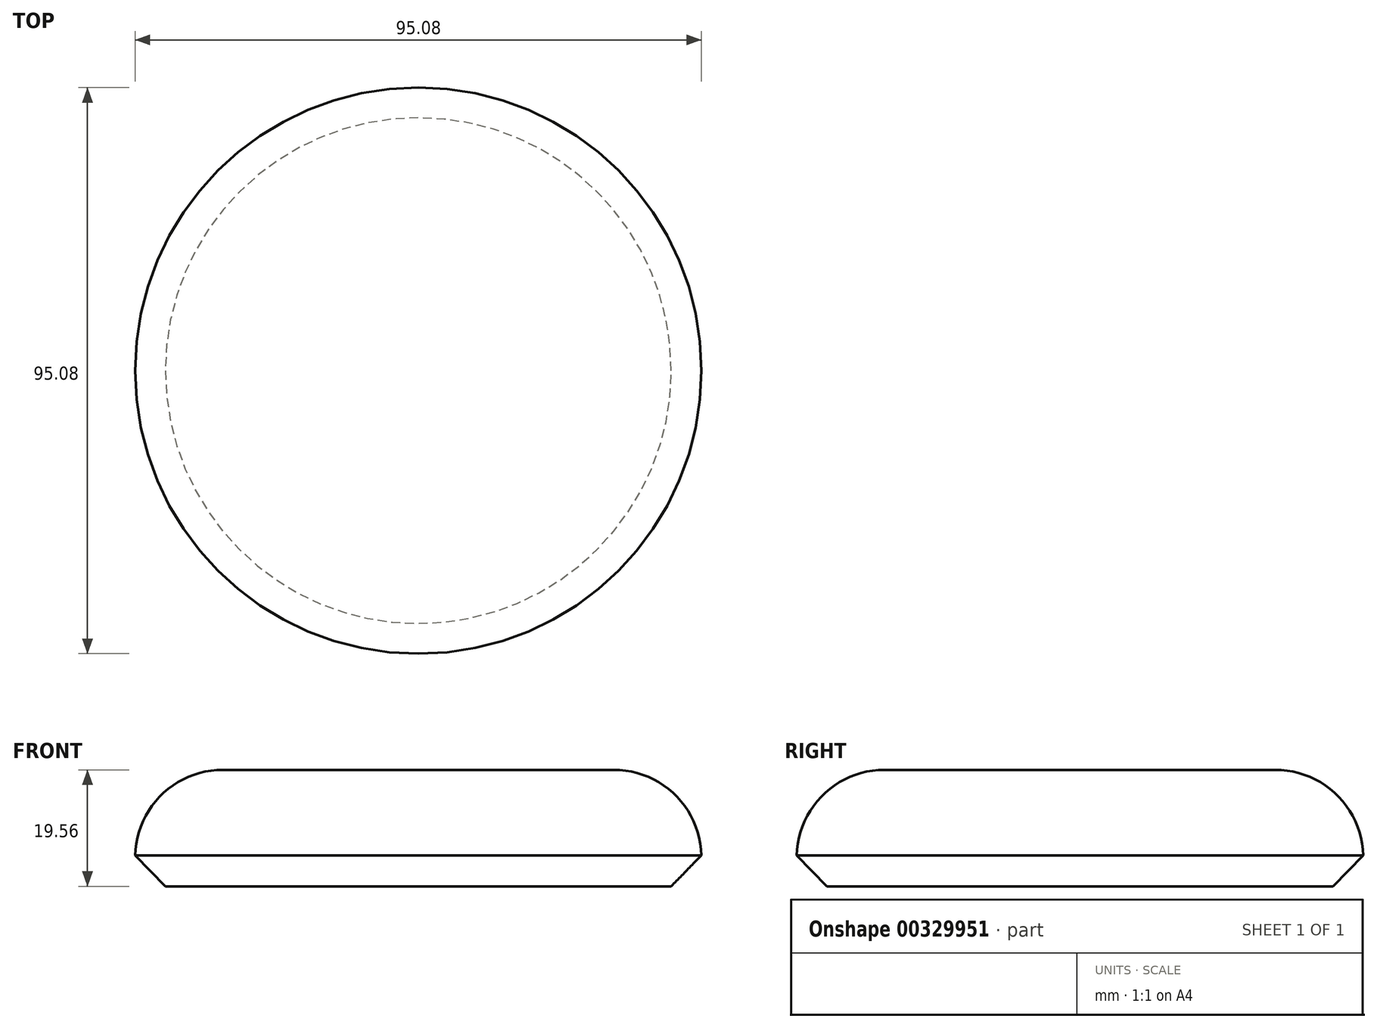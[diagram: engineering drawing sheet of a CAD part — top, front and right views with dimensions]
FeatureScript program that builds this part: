
annotation { "Feature Type Name" : "Feature", "Feature Type Description" : "" }
export const myFeature = defineFeature(function(context is Context, id is Id, definition is map)
    precondition{}
    {
        {
            var Q0;
            Q0=qCreatedBy(makeId("Top.planeOp"),FACE);
            var sketch = newSketch(context, id + "F0", { "sketchPlane" : qUnion([Q0])});
            skCircle(sketch, "E0", {"center": v(0, 0) * mm, "radius": 47.54 * mm});
            skSolve(sketch);
        }
        {
            var Q0;
            Q0=makeQuery(id+"F0.imprint","IMPRINT",FACE,{"disambiguationData":[TD([[makeQuery(id+"F0.imprint","IMPRINT",EDGE,{"derivedFrom":sQuery(id+"F0.wireOp",EDGE,"E0")}),1.0]])]});
            extrude(context, id + "F1", {"entities" : qUnion([Q0]), "depth" : 19.56 * mm});
        }
        {
            var Q0;
            Q0=makeQuery(id+"F1.opExtrude","CAP_FACE",FACE,{"disambiguationData":[OSD([sQuery(id+"F0.wireOp",EDGE,"E0")])],"isStart":false});
            fillet(context, id + "F2", {"entities" : qUnion([Q0]), "radius" : 14.72 * mm, "tangentPropagation" : true, "allowEdgeOverflow" : false});
        }
        {
            var Q0;
            Q0=makeQuery(id+"F1.opExtrude","SWEPT_FACE",FACE,{"disambiguationData":[OSD([sQuery(id+"F0.wireOp",EDGE,"E0")])]});
            chamfer(context, id + "F3", {"entities" : qUnion([Q0]), "width" : 5.08 * mm, "tangentPropagation" : true});
        }
    });
